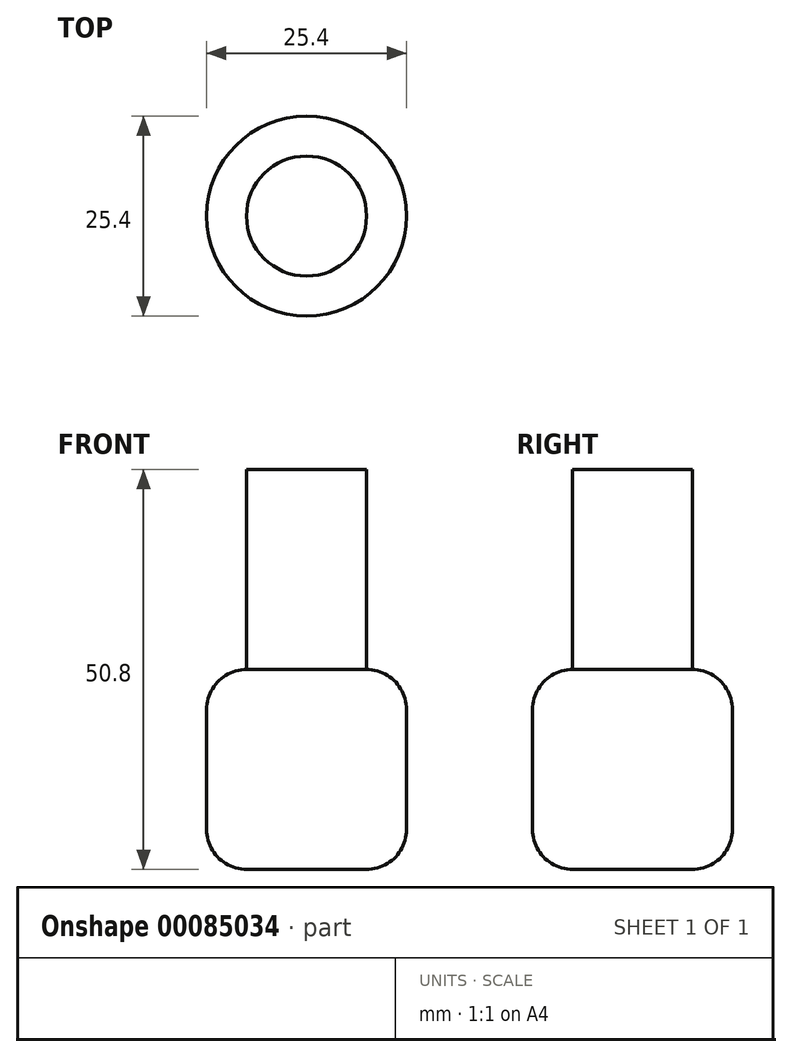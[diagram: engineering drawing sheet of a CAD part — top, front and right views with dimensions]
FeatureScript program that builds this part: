
annotation { "Feature Type Name" : "Feature", "Feature Type Description" : "" }
export const myFeature = defineFeature(function(context is Context, id is Id, definition is map)
    precondition{}
    {
        {
            var Q0;
            Q0=qCreatedBy(makeId("Top.planeOp"),FACE);
            var sketch = newSketch(context, id + "F0", { "sketchPlane" : qUnion([Q0])});
            skCircle(sketch, "E0", {"center": v(0, 0) * mm, "radius": 12.7 * mm});
            skSolve(sketch);
        }
        {
            var Q0;
            Q0=makeQuery(id+"F0.imprint","IMPRINT",FACE,{"disambiguationData":[TD([[makeQuery(id+"F0.imprint","IMPRINT",EDGE,{"derivedFrom":sQuery(id+"F0.wireOp",EDGE,"E0")}),1.0]])]});
            extrude(context, id + "F1", {"entities" : qUnion([Q0]), "depth" : 25.4 * mm});
        }
        {
            var Q0;
            Q0=makeQuery(id+"F1.opExtrude","CAP_EDGE",EDGE,{"disambiguationData":[OSD([sQuery(id+"F0.wireOp",EDGE,"E0")])],"isStart":false});
            var Q1;
            Q1=makeQuery(id+"F1.opExtrude","CAP_EDGE",EDGE,{"disambiguationData":[OSD([sQuery(id+"F0.wireOp",EDGE,"E0")])],"isStart":true});
            fillet(context, id + "F2", {"entities" : qUnion([Q0, Q1]), "radius" : 5.08 * mm, "tangentPropagation" : true, "allowEdgeOverflow" : false});
        }
        {
            var Q0;
            Q0=makeQuery(id+"F1.opExtrude","CAP_FACE",FACE,{"disambiguationData":[OSD([sQuery(id+"F0.wireOp",EDGE,"E0")])],"isStart":false});
            extrude(context, id + "F3", {"entities" : qUnion([Q0]), "operationType" : NewBodyOperationType.ADD, "depth" : 25.4 * mm});
        }
    });
